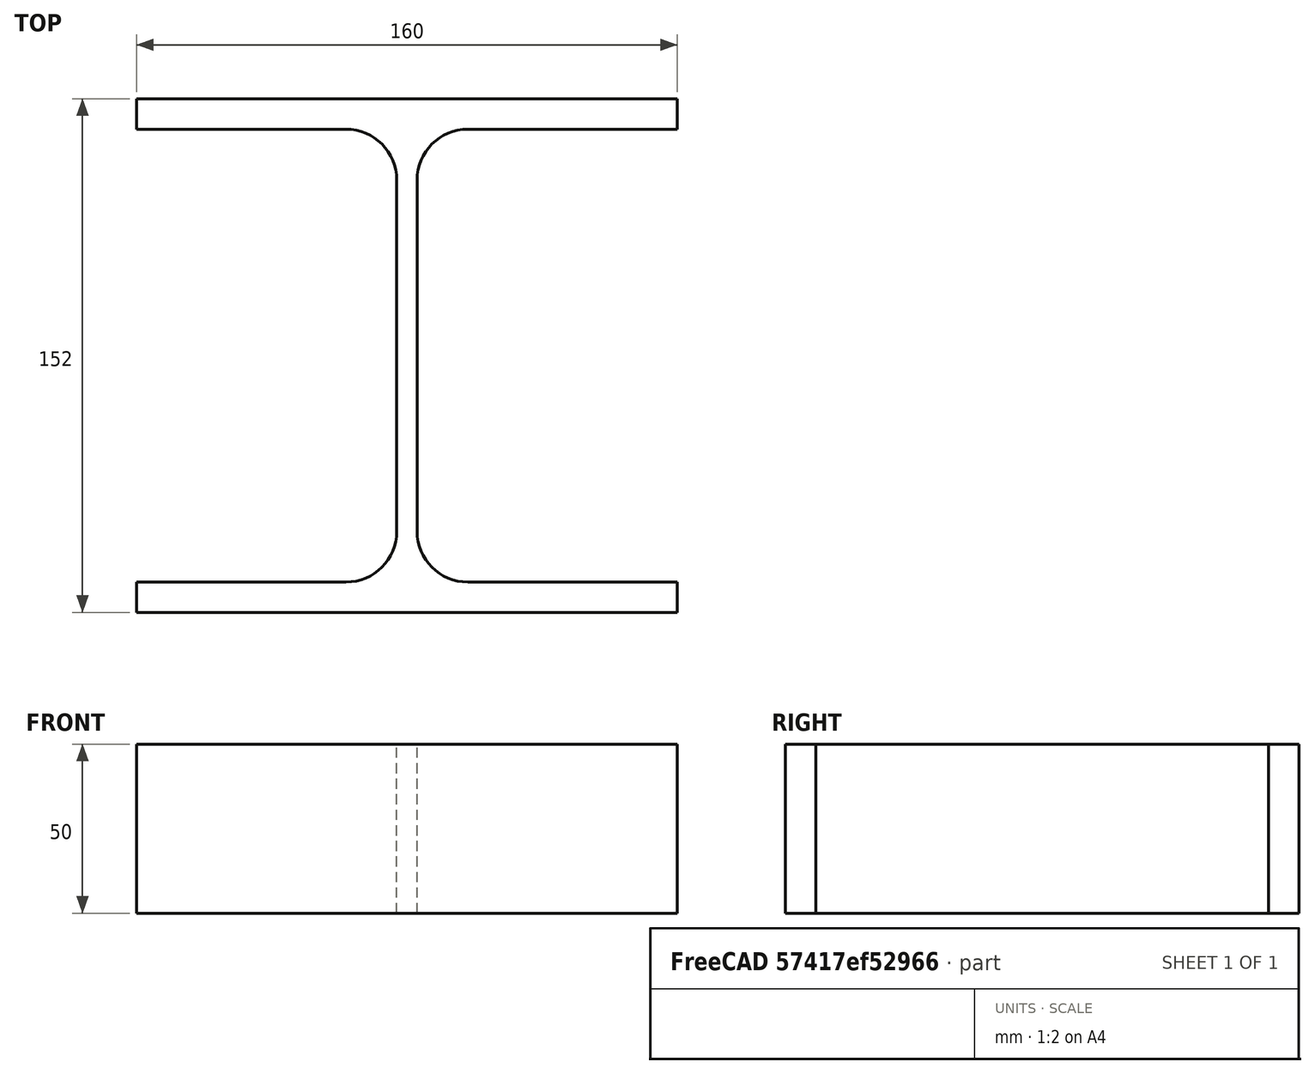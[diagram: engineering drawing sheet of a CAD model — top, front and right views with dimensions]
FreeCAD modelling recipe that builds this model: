
FCSTD DOCUMENT  (FreeCAD 0.15R4671 (Git))
Label: HE-A-Profile 160 DIN1025-3 S235JR
License: All rights reserved
LicenseURL: http://en.wikipedia.org/wiki/All_rights_reserved
objects: Sketcher::SketchObject×1, Part::Extrusion×1
note: 2 computed .brp shape members not serialized (recipe doc carries the construction recipe); baked Part::Feature solids carry a one-line shape summary decoded from their .brp

FEATURE [Sketcher::SketchObject] Sketch
  sketch-geometry (16):
    g0: LineSegment StartX=3 StartY=-52 StartZ=0 EndX=3 EndY=52 EndZ=0
    g1: LineSegment StartX=18 StartY=67 StartZ=0 EndX=80 EndY=67 EndZ=0
    g2: LineSegment StartX=80 StartY=67 StartZ=0 EndX=80 EndY=76 EndZ=0
    g3: LineSegment StartX=80 StartY=76 StartZ=0 EndX=-80 EndY=76 EndZ=0
    g4: LineSegment StartX=-80 StartY=76 StartZ=0 EndX=-80 EndY=67 EndZ=0
    g5: LineSegment StartX=-80 StartY=67 StartZ=0 EndX=-18 EndY=67 EndZ=0
    g6: LineSegment StartX=-3 StartY=52 StartZ=0 EndX=-3 EndY=-52 EndZ=0
    g7: LineSegment StartX=-18 StartY=-67 StartZ=0 EndX=-80 EndY=-67 EndZ=0
    g8: LineSegment StartX=-80 StartY=-67 StartZ=0 EndX=-80 EndY=-76 EndZ=0
    g9: LineSegment StartX=-80 StartY=-76 StartZ=0 EndX=80 EndY=-76 EndZ=0
    g10: LineSegment StartX=80 StartY=-76 StartZ=0 EndX=80 EndY=-67 EndZ=0
    g11: LineSegment StartX=80 StartY=-67 StartZ=0 EndX=18 EndY=-67 EndZ=0
    g12: ArcOfCircle CenterX=18 CenterY=52 CenterZ=0 NormalX=0 NormalY=0 NormalZ=1 Radius=15 StartAngle=1.5708 EndAngle=3.14159
    g13: ArcOfCircle CenterX=18 CenterY=-52 CenterZ=0 NormalX=0 NormalY=0 NormalZ=1 Radius=15 StartAngle=3.14159 EndAngle=4.71239
    g14: ArcOfCircle CenterX=-18 CenterY=52 CenterZ=0 NormalX=0 NormalY=0 NormalZ=1 Radius=15 StartAngle=0 EndAngle=1.5708
    g15: ArcOfCircle CenterX=-18 CenterY=-52 CenterZ=0 NormalX=0 NormalY=0 NormalZ=1 Radius=15 StartAngle=4.71239 EndAngle=6.28319
  constraints (42):
    c: Vertical(g0)
    c: Coincident(g2,g1)
    c: Vertical(g2)
    c: Coincident(g3,g2)
    c: Coincident(g4,g3)
    c: Vertical(g4)
    c: Coincident(g5,g4)
    c: Horizontal(g5)
    c: Vertical(g6)
    c: Horizontal(g7)
    c: Coincident(g8,g7)
    c: Vertical(g8)
    c: Coincident(g9,g8)
    c: Horizontal(g9)
    c: Coincident(g10,g9)
    c: Vertical(g10)
    c: Coincident(g11,g10)
    c: Horizontal(g11)
    c: Tangent(g1,g12) = 1.5708
    c: Tangent(g0,g12) = 1.5708
    c: Tangent(g0,g13) = 1.5708
    c: Tangent(g11,g13) = 1.5708
    c: Tangent(g5,g14) = 1.5708
    c: Tangent(g6,g14) = 1.5708
    c: Tangent(g6,g15) = 1.5708
    c: Tangent(g7,g15) = 1.5708
    c: Equal(g3,g9)
    c: Equal(g2,g4)
    c: Equal(g4,g8)
    c: Equal(g8,g10)
    c: Equal(g12,g14)
    c: Equal(g14,g15)
    c: Equal(g15,g13)
    c: Symmetric(g2,g3,g-2)
    c: Symmetric(g9,g8,g-2)
    c: Symmetric(g0,g6,g-2)
    c: Symmetric(g2,g9,g-1)
    c: DistanceY(g2,g9) = -152
    c: DistanceX(g3) = -160
    c: DistanceX(g0,g6) = -6
    c: DistanceY(g2) = 9
    c: Radius(g12) = 15
FEATURE [Part::Extrusion] Extrude  label="HE-A-Profile 160 DIN1025-3 S235JR"
  Base = -> Sketch
  Dir = (0,0,50)
  Solid = true
